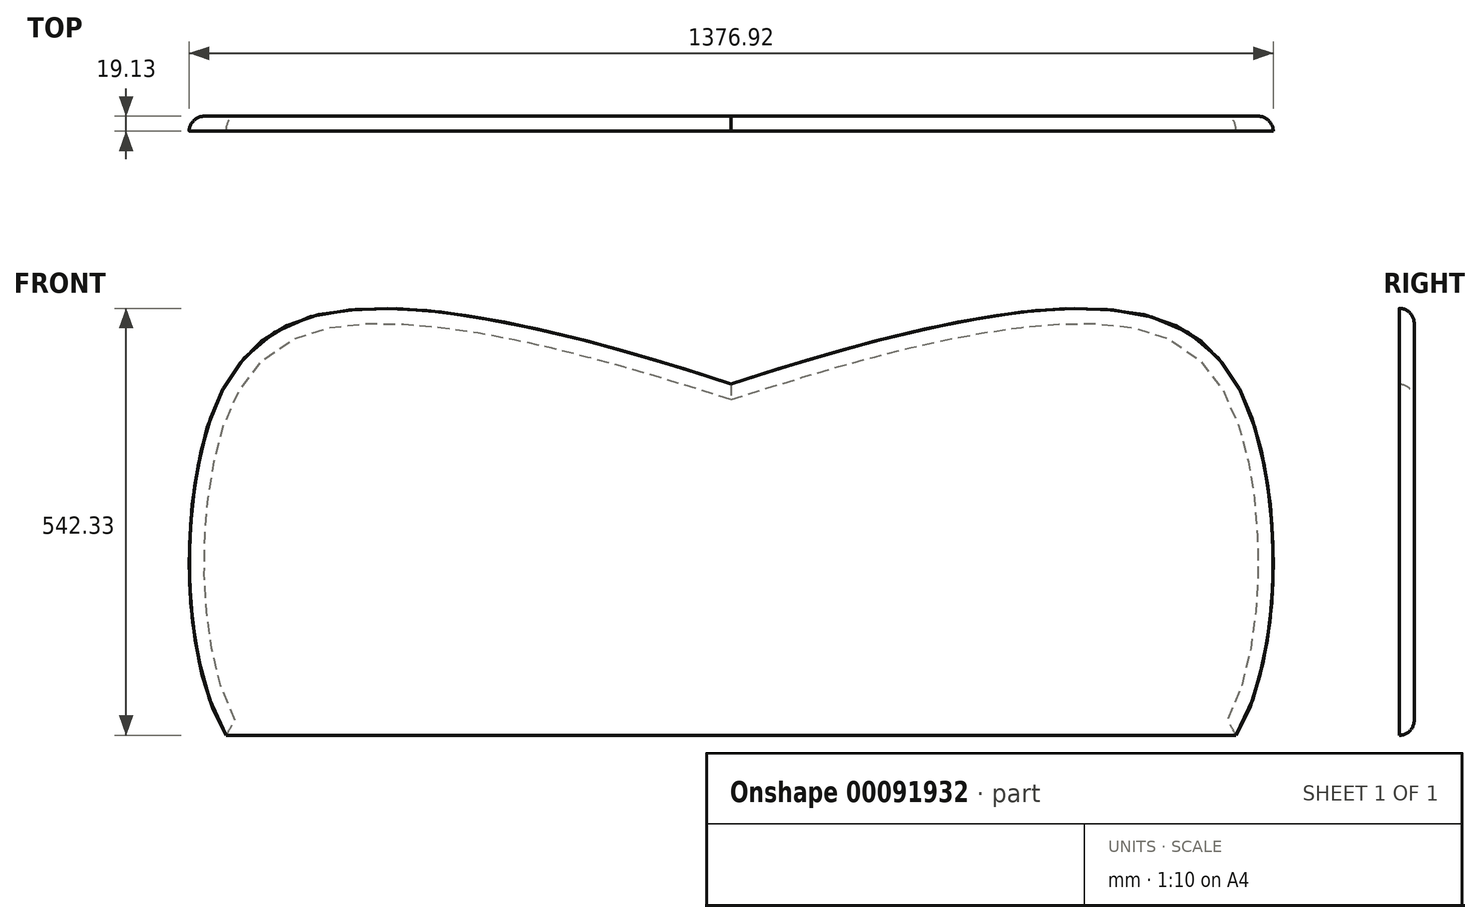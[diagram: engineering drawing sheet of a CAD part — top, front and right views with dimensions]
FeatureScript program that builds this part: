
annotation { "Feature Type Name" : "Feature", "Feature Type Description" : "" }
export const myFeature = defineFeature(function(context is Context, id is Id, definition is map)
    precondition{}
    {
        {
            var Q0;
            Q0=qCreatedBy(makeId("Front.planeOp"),FACE);
            var sketch = newSketch(context, id + "F0", { "sketchPlane" : qUnion([Q0])});
            skLineSegment(sketch, "E0", {"start": v(-641.35, -263.3) * mm, "end": v(641.35, -263.3) * mm});
            skFitSpline(sketch, "E1", {"points": [v(-641.35, -263.3) * mm, v(-679.2, 69.13) * mm, v(-541.5, 266.25) * mm, v(0, 183.08) * mm], "startDerivative": vector(-444.4, 728.97) * mm, "endDerivative": vector(1307.94, -425.2) * mm});
            skFitSpline(sketch, "E2.MirrorCS", {"points": [v(641.35, -263.3) * mm, v(679.2, 69.13) * mm, v(541.5, 266.25) * mm, v(0, 183.08) * mm], "startDerivative": vector(444.4, 728.97) * mm, "endDerivative": vector(-1307.94, -425.2) * mm});
            skLineSegment(sketch, "E3", {"start": v(-641.35, -263.3) * mm, "end": v(-641.35, 184.38) * mm, "construction": true});
            skLineSegment(sketch, "E4.MirrorCS", {"start": v(641.35, -263.3) * mm, "end": v(-641.35, -263.3) * mm});
            skLineSegment(sketch, "E5.MirrorCS", {"start": v(641.35, -263.3) * mm, "end": v(641.35, 184.38) * mm, "construction": true});
            skPoint(sketch, "E6", {"position": v(-479.64, 277.71) * mm});
            skPoint(sketch, "E7.MirrorP", {"position": v(479.64, 277.71) * mm});
            skSolve(sketch);
        }
        {
            var Q0;
            Q0=makeQuery(id+"F0.imprint","IMPRINT",FACE,{"disambiguationData":[TD([[makeQuery(id+"F0.imprint","IMPRINT",EDGE,{"derivedFrom":sQuery(id+"F0.wireOp",EDGE,"E1")}),-1.0]])]});
            extrude(context, id + "F1", {"entities" : qUnion([Q0]), "depth" : 19.13 * mm});
        }
        {
            var Q0;
            Q0=makeQuery(id+"F1.opExtrude","CAP_EDGE",EDGE,{"disambiguationData":[OSD([sQuery(id+"F0.wireOp",EDGE,"E0")])],"isStart":true});
            var Q1;
            Q1=makeQuery(id+"F1.opExtrude","CAP_EDGE",EDGE,{"disambiguationData":[OSD([sQuery(id+"F0.wireOp",EDGE,"E1")])],"isStart":true});
            var Q2;
            Q2=makeQuery(id+"F1.opExtrude","CAP_EDGE",EDGE,{"disambiguationData":[OSD([sQuery(id+"F0.wireOp",EDGE,"E2.MirrorCS")])],"isStart":true});
            fillet(context, id + "F2", {"entities" : qUnion([Q0, Q1, Q2]), "radius" : 19.05 * mm, "tangentPropagation" : true, "allowEdgeOverflow" : false});
        }
    });
